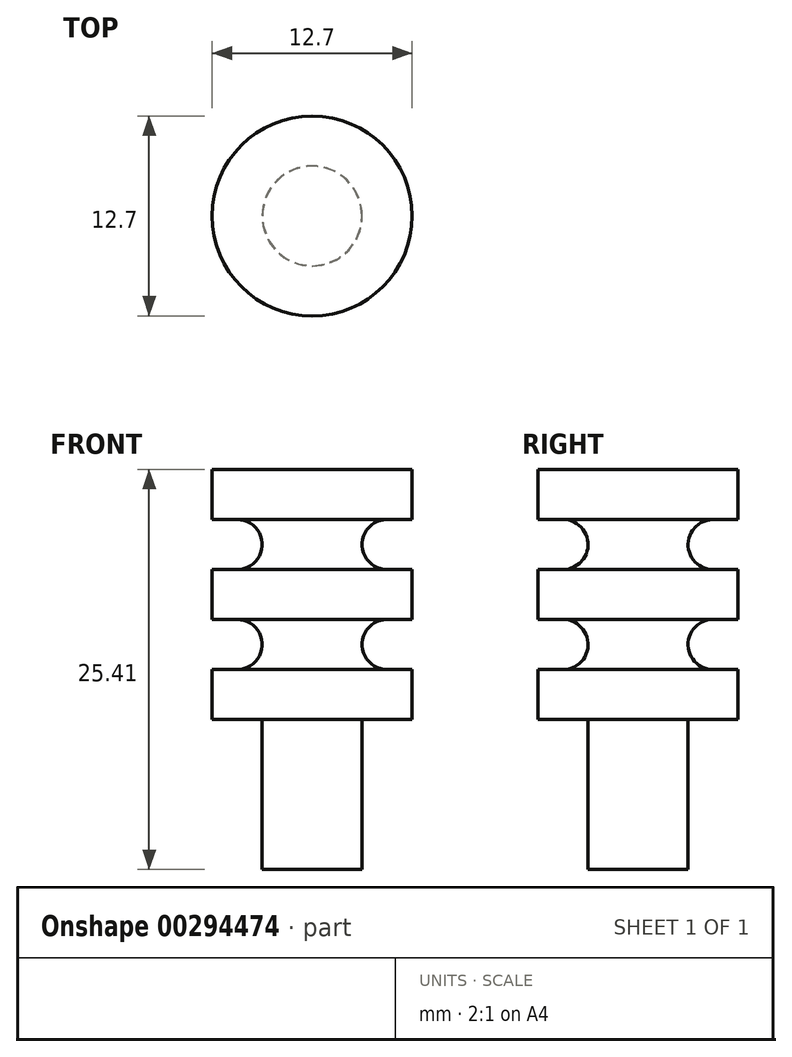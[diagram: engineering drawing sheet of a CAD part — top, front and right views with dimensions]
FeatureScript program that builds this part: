
annotation { "Feature Type Name" : "Feature", "Feature Type Description" : "" }
export const myFeature = defineFeature(function(context is Context, id is Id, definition is map)
    precondition{}
    {
        {
            var Q0;
            Q0=qCreatedBy(makeId("Top.planeOp"),FACE);
            var sketch = newSketch(context, id + "F0", { "sketchPlane" : qUnion([Q0])});
            skCircle(sketch, "E0", {"center": v(0, 0) * mm, "radius": 6.35 * mm});
            skCircle(sketch, "E1", {"center": v(0, 0) * mm, "radius": 3.18 * mm});
            skPoint(sketch, "E2", {"position": v(-6.35, 0) * mm});
            skPoint(sketch, "E3", {"position": v(0, 6.35) * mm});
            skSolve(sketch);
        }
        {
            var Q0;
            Q0=makeQuery(id+"F0.imprint","IMPRINT",FACE,{"disambiguationData":[TD([[makeQuery(id+"F0.imprint","IMPRINT",EDGE,{"derivedFrom":sQuery(id+"F0.wireOp",EDGE,"E0")}),1.0]])]});
            var Q1;
            Q1=makeQuery(id+"F0.imprint","IMPRINT",FACE,{"disambiguationData":[TD([[makeQuery(id+"F0.imprint","IMPRINT",EDGE,{"derivedFrom":sQuery(id+"F0.wireOp",EDGE,"E1")}),1.0]])]});
            extrude(context, id + "F1", {"entities" : qUnion([Q0, Q1]), "depth" : 15.88 * mm});
        }
        {
            var Q0;
            Q0=qCreatedBy(makeId("Front.planeOp"),FACE);
            var sketch = newSketch(context, id + "F2", { "sketchPlane" : qUnion([Q0])});
            skLineSegment(sketch, "E4", {"start": v(0, -76.4) * mm, "end": v(0, 75.84) * mm, "construction": true});
            skSolve(sketch);
        }
        {
            var Q0;
            Q0=makeQuery(id+"F0.imprint","IMPRINT",FACE,{"disambiguationData":[TD([[makeQuery(id+"F0.imprint","IMPRINT",EDGE,{"derivedFrom":sQuery(id+"F0.wireOp",EDGE,"E1")}),1.0]])]});
            extrude(context, id + "F3", {"entities" : qUnion([Q0]), "operationType" : NewBodyOperationType.ADD, "oppositeDirection" : true, "depth" : 9.52 * mm});
        }
        {
            var Q0;
            Q0=qCreatedBy(makeId("Right.planeOp"),FACE);
            var sketch = newSketch(context, id + "F4", { "sketchPlane" : qUnion([Q0])});
            skLineSegment(sketch, "E5.bottom", {"start": v(3.17, 6.35) * mm, "end": v(6.35, 6.35) * mm});
            skLineSegment(sketch, "E5.top", {"start": v(3.18, 3.17) * mm, "end": v(6.35, 3.18) * mm});
            skLineSegment(sketch, "E5.left", {"start": v(3.17, 6.35) * mm, "end": v(3.18, 3.17) * mm});
            skLineSegment(sketch, "E5.right", {"start": v(6.35, 6.35) * mm, "end": v(6.35, 3.18) * mm});
            skLineSegment(sketch, "E6.bottom", {"start": v(3.17, 12.7) * mm, "end": v(6.35, 12.7) * mm});
            skLineSegment(sketch, "E6.top", {"start": v(3.18, 9.53) * mm, "end": v(6.35, 9.53) * mm});
            skLineSegment(sketch, "E6.left", {"start": v(3.17, 12.7) * mm, "end": v(3.18, 9.53) * mm});
            skLineSegment(sketch, "E6.right", {"start": v(6.35, 12.7) * mm, "end": v(6.35, 9.53) * mm});
            skSolve(sketch);
        }
        {
            var Q0;
            Q0=qSketchRegion(id+"F4",true);
            var Q1;
            Q1=sQuery(id+"F2.wireOp",EDGE,"E4");
            revolve(context, id + "F5", {"operationType" : NewBodyOperationType.REMOVE, "entities" : qUnion([Q0]), "axis" : qUnion([Q1]), "revolveType" : RevolveType.FULL, "oppositeDirection" : true});
        }
        {
            var Q0;
            Q0=makeQuery(id+"F5.boolean.opBoolean","COPY",EDGE,{"derivedFrom":makeQuery(id+"F5.opRevolve","SWEPT_EDGE",EDGE,{"disambiguationData":[OSD([sQuery(id+"F4.wireOp",EDGE,"E5.top"),sQuery(id+"F4.wireOp",EDGE,"E5.left")])]})});
            var Q1;
            Q1=makeQuery(id+"F5.boolean.opBoolean","COPY",EDGE,{"derivedFrom":makeQuery(id+"F5.opRevolve","SWEPT_EDGE",EDGE,{"disambiguationData":[OSD([sQuery(id+"F4.wireOp",EDGE,"E5.bottom"),sQuery(id+"F4.wireOp",EDGE,"E5.left")])]})});
            var Q2;
            Q2=makeQuery(id+"F5.boolean.opBoolean","COPY",EDGE,{"derivedFrom":makeQuery(id+"F5.opRevolve","SWEPT_EDGE",EDGE,{"disambiguationData":[OSD([sQuery(id+"F4.wireOp",EDGE,"E6.top"),sQuery(id+"F4.wireOp",EDGE,"E6.left")])]})});
            var Q3;
            Q3=makeQuery(id+"F5.boolean.opBoolean","COPY",EDGE,{"derivedFrom":makeQuery(id+"F5.opRevolve","SWEPT_EDGE",EDGE,{"disambiguationData":[OSD([sQuery(id+"F4.wireOp",EDGE,"E6.bottom"),sQuery(id+"F4.wireOp",EDGE,"E6.left")])]})});
            fillet(context, id + "F6", {"entities" : qUnion([Q0, Q1, Q2, Q3]), "radius" : 1.59 * mm, "tangentPropagation" : true, "allowEdgeOverflow" : false});
        }
    });
